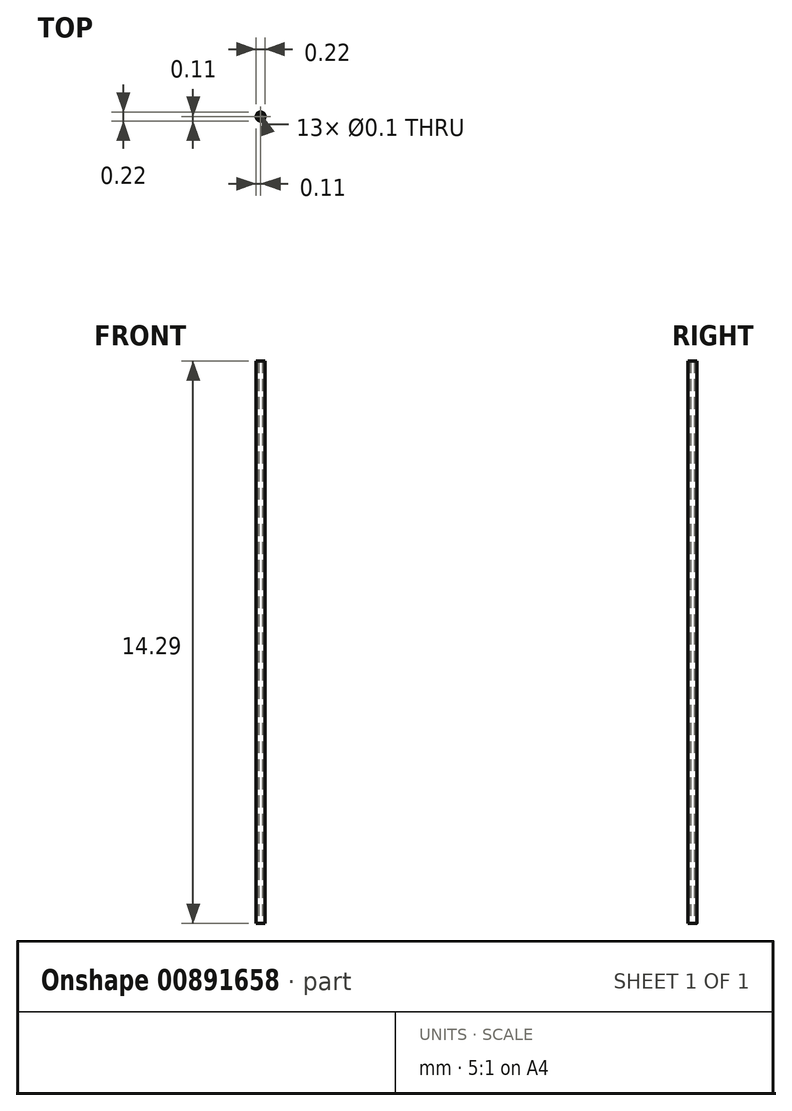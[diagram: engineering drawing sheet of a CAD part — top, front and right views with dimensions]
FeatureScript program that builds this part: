
annotation { "Feature Type Name" : "Feature", "Feature Type Description" : "" }
export const myFeature = defineFeature(function(context is Context, id is Id, definition is map)
    precondition{}
    {
        {
            var Q0;
            Q0=qCreatedBy(makeId("Top.planeOp"),FACE);
            var sketch = newSketch(context, id + "F0", { "sketchPlane" : qUnion([Q0])});
            skCircle(sketch, "E0", {"center": v(0, 0) * mm, "radius": 0.11 * mm});
            skCircle(sketch, "E1", {"center": v(0, 0) * mm, "radius": 0.05 * mm});
            skSolve(sketch);
        }
        {
            var Q0;
            Q0=makeQuery(id+"F0.imprint","IMPRINT",FACE,{"disambiguationData":[TD([[makeQuery(id+"F0.imprint","IMPRINT",EDGE,{"derivedFrom":sQuery(id+"F0.wireOp",EDGE,"E0")}),1.0]])]});
            extrude(context, id + "F1", {"entities" : qUnion([Q0]), "depth" : 14.29 * mm, "offsetDistance" : 25.4 * mm});
        }
    });
